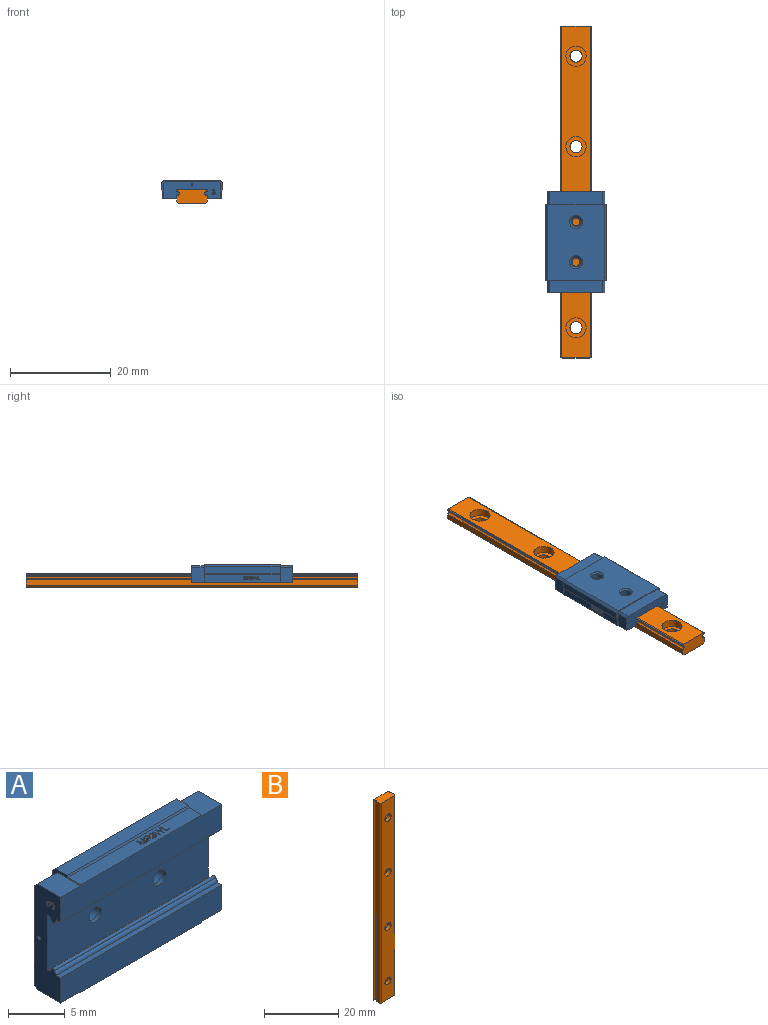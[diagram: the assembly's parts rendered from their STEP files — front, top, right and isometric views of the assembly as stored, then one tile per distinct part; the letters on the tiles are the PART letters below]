
ASSEMBLY  parts=2 mates=1
PART A: 248 faces, bbox 20.1x3.5x12 mm
  f0: cone r=1.3mm half-angle=45deg, axis (0,1,0), area 3.1mm2, adj f2,f9
  f1: cone r=1.3mm half-angle=45deg, axis (0,1,0), area 3.1mm2, adj f3,f9
  f2: cylinder r=1mm len=2mm, axis (0,1,0), area 6.9mm2, adj f0,f32
  f3: cylinder r=1mm len=2mm, axis (0,1,0), area 6.9mm2, adj f1,f33
  f4: cylinder r=0.15mm len=3mm, axis (-1,0,0), area 2.8mm2, adj f23,f76
  f5: cylinder r=0.15mm len=3mm, axis (1,0,0), area 2.8mm2, adj f28,f222
  f6: cylinder r=0.8mm len=1.6mm, axis (0,1,0), area 2mm2, adj f32,f51
  f7: cylinder r=0.8mm len=1.6mm, axis (0,1,0), area 2mm2, adj f33,f51
  f8: cylinder r=0.15mm len=20.1mm, axis (1,0,0), area 10.6mm2, adj f23,f28,f148,f223
  f9: plane 15.1x11.2mm, normal (0,1,0), area 158.5mm2, adj f0,f1,f10,f11,f12,f13
  f10: plane 12x3.5mm, normal (-1,0,0), area 3.7mm2, adj f9,f11,f13,f14,f15,f16,f17,f21
  f11: plane 15.1x0.4mm, normal (0,0.71,-0.71), area 8.5mm2, adj f9,f10,f12,f17
  f12: plane 12x3.5mm, normal (1,0,0), area 3.7mm2, adj f9,f11,f13,f17,f18,f19,f20,f21
  f13: plane 15.1x0.4mm, normal (0,0.71,0.71), area 8.5mm2, adj f9,f10,f12,f21
  f14: plane 2.9x2.5mm, normal (0,0,1), area 7.3mm2, adj f10,f22,f23,f24
  f15: plane 10.6x2.5mm, normal (0,1,0), area 26.5mm2, adj f10,f22,f23,f25
  f16: plane 2.9x2.5mm, normal (0,0,-1), area 7.3mm2, adj f10,f23,f25,f26
  f17: plane 15.1x1.4mm, normal (0,0,-1), area 21.1mm2, adj f10,f11,f12,f27
  f18: plane 2.9x2.5mm, normal (0,0,-1), area 7.3mm2, adj f12,f26,f28,f29
  f19: plane 2.9x2.5mm, normal (0,0,1), area 7.3mm2, adj f12,f24,f28,f30
  f20: plane 10.6x2.5mm, normal (0,1,0), area 26.5mm2, adj f12,f28,f29,f30
  f21: plane 15.1x1.4mm, normal (0,0,1), area 21.1mm2, adj f10,f12,f13,f31
  f22: plane 2.5x0.4mm, normal (0,0.71,0.71), area 1.4mm2, adj f10,f14,f15,f23
  f23: plane 11.4x3.3mm, normal (-1,0,0), area 27.5mm2, adj f4,f8,f14,f15,f16,f22,f24,f25
  f24: plane 20.1x2.8mm, normal (0,-1,0), area 55.8mm2, adj f10,f12,f14,f19,f23,f28,f52,f53
  f25: plane 2.5x0.4mm, normal (0,0.71,-0.71), area 1.4mm2, adj f10,f15,f16,f23
  f26: plane 20.1x2.8mm, normal (0,-1,0), area 55.8mm2, adj f10,f12,f16,f18,f23,f28,f54,f55
  f27: plane 15.1x0.2mm, normal (0,-0.87,-0.5), area 3.5mm2, adj f10,f12,f17,f54
  f28: plane 11.4x3.3mm, normal (1,0,0), area 27.5mm2, adj f5,f8,f18,f19,f20,f24,f26,f29
  f29: plane 2.5x0.4mm, normal (0,0.71,-0.71), area 1.4mm2, adj f12,f18,f20,f28
  f30: plane 2.5x0.4mm, normal (0,0.71,0.71), area 1.4mm2, adj f12,f19,f20,f28
  f31: plane 15.1x0.2mm, normal (0,-0.87,0.5), area 3.5mm2, adj f10,f12,f21,f52
  f32: plane 2x2mm, normal (0,1,0), area 1.1mm2, adj f2,f6
  f33: plane 2x2mm, normal (0,1,0), area 1.1mm2, adj f3,f7
  f34: bspline ~0.32x0.29mm, area 0.1mm2, adj f23,f35,f50,f73
  f35: plane 0.2x0.13mm, normal (0,-1,0.1), area 0mm2, adj f23,f34,f36,f73
  f36: bspline ~0.2x0.19mm, area 0.1mm2, adj f23,f35,f37,f73
  f37: bspline ~0.2x0.2mm, area 0.1mm2, adj f23,f36,f38,f73
  f38: bspline ~0.2x0.19mm, area 0.1mm2, adj f23,f37,f39,f73
  f39: bspline ~0.2x0.09mm, area 0mm2, adj f23,f38,f40,f73
  f40: plane 0.2x0.12mm, normal (0,-0.11,0.99), area 0mm2, adj f23,f39,f41,f73
  f41: bspline ~0.2x0.02mm, area 0mm2, adj f23,f40,f42,f73
  f42: bspline ~0.2x0.19mm, area 0.1mm2, adj f23,f41,f43,f73
  f43: bspline ~0.2x0.16mm, area 0mm2, adj f23,f42,f44,f73
  f44: bspline ~0.2x0.17mm, area 0.1mm2, adj f23,f43,f45,f73
  f45: plane 0.2x0.13mm, normal (0,1,0.1), area 0mm2, adj f23,f44,f46,f73
  f46: bspline ~0.3x0.26mm, area 0.1mm2, adj f23,f45,f47,f73
  f47: bspline ~0.29x0.26mm, area 0.1mm2, adj f23,f46,f48,f73
  f48: bspline ~0.2x0.2mm, area 0.1mm2, adj f23,f47,f49,f73
  f49: bspline ~0.25x0.2mm, area 0.1mm2, adj f23,f48,f50,f73
  f50: bspline ~0.34x0.32mm, area 0.1mm2, adj f23,f34,f49,f73
  f51: plane 20.1x6mm, normal (0,-1,0), area 116.6mm2, adj f6,f7,f23,f28,f74,f75
  f52: plane 15.1x1.58mm, normal (0,0,1), area 23mm2, adj f10,f12,f24,f31,f77,f78,f79,f80
  f53: plane 20.1x0.55mm, normal (0,0,-1), area 11.1mm2, adj f23,f24,f28,f148
  f54: plane 15.1x1.58mm, normal (0,0,-1), area 23mm2, adj f10,f12,f26,f27,f149,f150,f151,f152
  f55: plane 20.1x0.55mm, normal (0,0,1), area 11.1mm2, adj f23,f26,f28,f220
  f56: bspline ~0.32x0.29mm, area 0.1mm2, adj f28,f57,f72,f221
  f57: plane 0.2x0.13mm, normal (0,-1,-0.1), area 0mm2, adj f28,f56,f58,f221
  f58: bspline ~0.2x0.19mm, area 0.1mm2, adj f28,f57,f59,f221
  f59: bspline ~0.2x0.2mm, area 0.1mm2, adj f28,f58,f60,f221
  f60: bspline ~0.2x0.19mm, area 0.1mm2, adj f28,f59,f61,f221
  f61: bspline ~0.2x0.09mm, area 0mm2, adj f28,f60,f62,f221
  f62: plane 0.2x0.12mm, normal (0,-0.11,-0.99), area 0mm2, adj f28,f61,f63,f221
  f63: bspline ~0.2x0.02mm, area 0mm2, adj f28,f62,f64,f221
  f64: bspline ~0.2x0.19mm, area 0.1mm2, adj f28,f63,f65,f221
  f65: bspline ~0.2x0.16mm, area 0mm2, adj f28,f64,f66,f221
  f66: bspline ~0.2x0.17mm, area 0.1mm2, adj f28,f65,f67,f221
  f67: plane 0.2x0.13mm, normal (0,1,-0.1), area 0mm2, adj f28,f66,f68,f221
  f68: bspline ~0.3x0.26mm, area 0.1mm2, adj f28,f67,f69,f221
  f69: bspline ~0.29x0.26mm, area 0.1mm2, adj f28,f68,f70,f221
  f70: bspline ~0.2x0.2mm, area 0.1mm2, adj f28,f69,f71,f221
  f71: bspline ~0.25x0.2mm, area 0.1mm2, adj f28,f70,f72,f221
  f72: bspline ~0.34x0.32mm, area 0.1mm2, adj f28,f56,f71,f221
  f73: plane 1.04x0.66mm, normal (-1,0,0), area 0.3mm2, adj f34,f35,f36,f37,f38,f39,f40,f41
  f74: plane 20.1x0.35mm, normal (0,0,-1), area 7mm2, adj f23,f28,f51,f223
  f75: plane 20.1x0.35mm, normal (0,0,1), area 7mm2, adj f23,f28,f51,f224
  f76: plane 0.3x0.3mm, normal (-1,0,0), area 0.1mm2, adj f4
  f77: plane 0.33x0.15mm, normal (0,-1,0), area 0mm2, adj f52,f78,f82,f225
  f78: plane 0.62x0.15mm, normal (-1,0,0), area 0.1mm2, adj f52,f77,f79,f225
  f79: plane 0.15x0.1mm, normal (0,-1,0), area 0mm2, adj f52,f78,f80,f225
  f80: plane 0.7x0.15mm, normal (1,0,0), area 0.1mm2, adj f52,f79,f81,f225
  f81: plane 0.43x0.15mm, normal (0,1,0), area 0.1mm2, adj f52,f80,f82,f225
  f82: plane 0.15x0.08mm, normal (-1,0,0), area 0mm2, adj f52,f77,f81,f225
  f83: bspline ~0.17x0.15mm, area 0mm2, adj f52,f84,f99,f226
  f84: bspline ~0.15x0.14mm, area 0mm2, adj f52,f83,f85,f226
  f85: bspline ~0.2x0.18mm, area 0mm2, adj f52,f84,f86,f226
  f86: bspline ~0.2x0.18mm, area 0mm2, adj f52,f85,f87,f226
  f87: plane 0.15x0.09mm, normal (0.1,1,0), area 0mm2, adj f52,f86,f88,f226
  f88: bspline ~0.15x0.12mm, area 0mm2, adj f52,f87,f89,f226
  f89: bspline ~0.15x0.11mm, area 0mm2, adj f52,f88,f90,f226
  f90: bspline ~0.15x0.13mm, area 0mm2, adj f52,f89,f91,f226
  f91: bspline ~0.15x0.01mm, area 0mm2, adj f52,f90,f92,f226
  f92: plane 0.15x0.08mm, normal (0.99,-0.11,0), area 0mm2, adj f52,f91,f93,f226
  f93: bspline ~0.15x0.06mm, area 0mm2, adj f52,f92,f94,f226
  f94: bspline ~0.15x0.13mm, area 0mm2, adj f52,f93,f95,f226
  f95: bspline ~0.15x0.14mm, area 0mm2, adj f52,f94,f96,f226
  f96: bspline ~0.15x0.13mm, area 0mm2, adj f52,f95,f97,f226
  f97: plane 0.15x0.09mm, normal (0.1,-1,0), area 0mm2, adj f52,f96,f98,f226
  f98: bspline ~0.22x0.2mm, area 0mm2, adj f52,f97,f99,f226
  f99: bspline ~0.23x0.22mm, area 0.1mm2, adj f52,f83,f98,f226
  f100: plane 0.59x0.19mm, normal (0.95,0.3,0), area 0.1mm2, adj f52,f101,f114,f227
  f101: plane 0.15x0.1mm, normal (0,1,0), area 0mm2, adj f52,f100,f102,f227
  f102: plane 0.59x0.19mm, normal (-0.95,0.3,0), area 0.1mm2, adj f52,f101,f103,f227
  f103: plane 0.59x0.15mm, normal (1,0,0), area 0.1mm2, adj f52,f102,f104,f227
  f104: plane 0.15x0.1mm, normal (0,1,0), area 0mm2, adj f52,f103,f105,f227
  f105: plane 0.7x0.15mm, normal (-1,0,0), area 0.1mm2, adj f52,f104,f106,f227
  f106: plane 0.15x0.15mm, normal (0,-1,0), area 0mm2, adj f52,f105,f107,f227
  f107: plane 0.48x0.16mm, normal (0.95,-0.31,0), area 0.1mm2, adj f52,f106,f108,f227
  f108: bspline ~0.15x0.11mm, area 0mm2, adj f52,f107,f109,f227
  f109: bspline ~0.15x0.1mm, area 0mm2, adj f52,f108,f110,f227
  f110: plane 0.49x0.16mm, normal (-0.95,-0.3,0), area 0.1mm2, adj f52,f109,f111,f227
  f111: plane 0.15x0.15mm, normal (0,-1,0), area 0mm2, adj f52,f110,f112,f227
  f112: plane 0.7x0.15mm, normal (1,0,0), area 0.1mm2, adj f52,f111,f113,f227
  f113: plane 0.15x0.1mm, normal (0,1,0), area 0mm2, adj f52,f112,f114,f227
  f114: plane 0.59x0.15mm, normal (-1,0,0), area 0.1mm2, adj f52,f100,f113,f227
  f115: plane 0.15x0.1mm, normal (0,1,0), area 0mm2, adj f52,f116,f128,f228
  f116: bspline ~0.15x0.05mm, area 0mm2, adj f52,f115,f117,f228
  f117: bspline ~0.16x0.15mm, area 0mm2, adj f52,f116,f118,f228
  f118: plane 0.15x0.15mm, normal (0.86,0.51,0), area 0mm2, adj f52,f117,f119,f228
  f119: plane 0.15x0.11mm, normal (0,1,0), area 0mm2, adj f52,f118,f120,f228
  f120: plane 0.19x0.15mm, normal (-0.86,-0.51,0), area 0mm2, adj f52,f119,f121,f228
  f121: bspline ~0.15x0.1mm, area 0mm2, adj f52,f120,f122,f228
  f122: bspline ~0.15x0.05mm, area 0mm2, adj f52,f121,f123,f228
  f123: bspline ~0.19x0.19mm, area 0mm2, adj f52,f122,f124,f228
  f124: bspline ~0.23x0.19mm, area 0.1mm2, adj f52,f123,f125,f228
  f125: plane 0.3x0.15mm, normal (0,-1,0), area 0mm2, adj f52,f124,f126,f228
  f126: plane 0.7x0.15mm, normal (1,0,0), area 0.1mm2, adj f52,f125,f127,f228
  f127: plane 0.15x0.1mm, normal (0,1,0), area 0mm2, adj f52,f126,f128,f228
  f128: plane 0.31x0.15mm, normal (-1,0,0), area 0mm2, adj f52,f115,f127,f228
  f129: bspline ~0.15x0.09mm, area 0mm2, adj f52,f130,f147,f229
  f130: bspline ~0.15x0.08mm, area 0mm2, adj f52,f129,f131,f229
  f131: plane 0.54x0.15mm, normal (0.96,0.26,0), area 0.1mm2, adj f52,f130,f132,f229
  f132: plane 0.15x0.11mm, normal (0,1,0), area 0mm2, adj f52,f131,f133,f229
  f133: plane 0.7x0.18mm, normal (-0.97,0.24,0), area 0.1mm2, adj f52,f132,f134,f229
  f134: plane 0.15x0.1mm, normal (0,-1,0), area 0mm2, adj f52,f133,f135,f229
  f135: plane 0.46x0.15mm, normal (0.98,-0.22,0), area 0.1mm2, adj f52,f134,f136,f229
  f136: bspline ~0.15x0.14mm, area 0mm2, adj f52,f135,f137,f229
  f137: bspline ~0.25x0.15mm, area 0mm2, adj f52,f136,f138,f229
  f138: plane 0.35x0.15mm, normal (-0.96,-0.27,0), area 0.1mm2, adj f52,f137,f139,f229
  f139: plane 0.15x0.12mm, normal (0,-1,0), area 0mm2, adj f52,f138,f140,f229
  f140: plane 0.48x0.15mm, normal (0.96,-0.28,0), area 0.1mm2, adj f52,f139,f141,f229
  f141: bspline ~0.15x0.12mm, area 0mm2, adj f52,f140,f142,f229
  f142: bspline ~0.15x0.14mm, area 0mm2, adj f52,f141,f143,f229
  f143: plane 0.46x0.15mm, normal (-0.98,-0.22,0), area 0.1mm2, adj f52,f142,f144,f229
  f144: plane 0.15x0.1mm, normal (0,-1,0), area 0mm2, adj f52,f143,f145,f229
  f145: plane 0.7x0.18mm, normal (0.97,0.24,0), area 0.1mm2, adj f52,f144,f146,f229
  f146: plane 0.15x0.12mm, normal (0,1,0), area 0mm2, adj f52,f145,f147,f229
  f147: plane 0.52x0.15mm, normal (-0.96,0.28,0), area 0.1mm2, adj f52,f129,f146,f229
  f148: cylinder r=0.4mm len=20.1mm, axis (1,0,0), area 9.6mm2, adj f8,f23,f28,f53
  f149: plane 0.33x0.15mm, normal (0,-1,0), area 0mm2, adj f54,f150,f154,f230
  f150: plane 0.62x0.15mm, normal (1,0,0), area 0.1mm2, adj f54,f149,f151,f230
  f151: plane 0.15x0.1mm, normal (0,-1,0), area 0mm2, adj f54,f150,f152,f230
  f152: plane 0.7x0.15mm, normal (-1,0,0), area 0.1mm2, adj f54,f151,f153,f230
  f153: plane 0.43x0.15mm, normal (0,1,0), area 0.1mm2, adj f54,f152,f154,f230
  f154: plane 0.15x0.08mm, normal (1,0,0), area 0mm2, adj f54,f149,f153,f230
  f155: bspline ~0.17x0.15mm, area 0mm2, adj f54,f156,f171,f231
  f156: bspline ~0.15x0.14mm, area 0mm2, adj f54,f155,f157,f231
  f157: bspline ~0.2x0.18mm, area 0mm2, adj f54,f156,f158,f231
  f158: bspline ~0.2x0.18mm, area 0mm2, adj f54,f157,f159,f231
  f159: plane 0.15x0.09mm, normal (-0.1,1,0), area 0mm2, adj f54,f158,f160,f231
  f160: bspline ~0.15x0.12mm, area 0mm2, adj f54,f159,f161,f231
  f161: bspline ~0.15x0.11mm, area 0mm2, adj f54,f160,f162,f231
  f162: bspline ~0.15x0.13mm, area 0mm2, adj f54,f161,f163,f231
  f163: bspline ~0.15x0.01mm, area 0mm2, adj f54,f162,f164,f231
  f164: plane 0.15x0.08mm, normal (-0.99,-0.11,0), area 0mm2, adj f54,f163,f165,f231
  f165: bspline ~0.15x0.06mm, area 0mm2, adj f54,f164,f166,f231
  f166: bspline ~0.15x0.13mm, area 0mm2, adj f54,f165,f167,f231
  f167: bspline ~0.15x0.14mm, area 0mm2, adj f54,f166,f168,f231
  f168: bspline ~0.15x0.13mm, area 0mm2, adj f54,f167,f169,f231
  f169: plane 0.15x0.09mm, normal (-0.1,-1,0), area 0mm2, adj f54,f168,f170,f231
  f170: bspline ~0.22x0.2mm, area 0mm2, adj f54,f169,f171,f231
  f171: bspline ~0.23x0.22mm, area 0.1mm2, adj f54,f155,f170,f231
  f172: plane 0.59x0.19mm, normal (-0.95,0.3,0), area 0.1mm2, adj f54,f173,f186,f232
  f173: plane 0.15x0.1mm, normal (0,1,0), area 0mm2, adj f54,f172,f174,f232
  f174: plane 0.59x0.19mm, normal (0.95,0.3,0), area 0.1mm2, adj f54,f173,f175,f232
  f175: plane 0.59x0.15mm, normal (-1,0,0), area 0.1mm2, adj f54,f174,f176,f232
  f176: plane 0.15x0.1mm, normal (0,1,0), area 0mm2, adj f54,f175,f177,f232
  f177: plane 0.7x0.15mm, normal (1,0,0), area 0.1mm2, adj f54,f176,f178,f232
  f178: plane 0.15x0.15mm, normal (0,-1,0), area 0mm2, adj f54,f177,f179,f232
  f179: plane 0.48x0.16mm, normal (-0.95,-0.31,0), area 0.1mm2, adj f54,f178,f180,f232
  f180: bspline ~0.15x0.11mm, area 0mm2, adj f54,f179,f181,f232
  f181: bspline ~0.15x0.1mm, area 0mm2, adj f54,f180,f182,f232
  f182: plane 0.49x0.16mm, normal (0.95,-0.3,0), area 0.1mm2, adj f54,f181,f183,f232
  f183: plane 0.15x0.15mm, normal (0,-1,0), area 0mm2, adj f54,f182,f184,f232
  f184: plane 0.7x0.15mm, normal (-1,0,0), area 0.1mm2, adj f54,f183,f185,f232
  f185: plane 0.15x0.1mm, normal (0,1,0), area 0mm2, adj f54,f184,f186,f232
  f186: plane 0.59x0.15mm, normal (1,0,0), area 0.1mm2, adj f54,f172,f185,f232
  f187: plane 0.15x0.1mm, normal (0,1,0), area 0mm2, adj f54,f188,f200,f233
  f188: bspline ~0.15x0.05mm, area 0mm2, adj f54,f187,f189,f233
  f189: bspline ~0.16x0.15mm, area 0mm2, adj f54,f188,f190,f233
  f190: plane 0.15x0.15mm, normal (-0.86,0.51,0), area 0mm2, adj f54,f189,f191,f233
  f191: plane 0.15x0.11mm, normal (0,1,0), area 0mm2, adj f54,f190,f192,f233
  f192: plane 0.19x0.15mm, normal (0.86,-0.51,0), area 0mm2, adj f54,f191,f193,f233
  f193: bspline ~0.15x0.1mm, area 0mm2, adj f54,f192,f194,f233
  f194: bspline ~0.15x0.05mm, area 0mm2, adj f54,f193,f195,f233
  f195: bspline ~0.19x0.19mm, area 0mm2, adj f54,f194,f196,f233
  f196: bspline ~0.23x0.19mm, area 0.1mm2, adj f54,f195,f197,f233
  f197: plane 0.3x0.15mm, normal (0,-1,0), area 0mm2, adj f54,f196,f198,f233
  f198: plane 0.7x0.15mm, normal (-1,0,0), area 0.1mm2, adj f54,f197,f199,f233
  f199: plane 0.15x0.1mm, normal (0,1,0), area 0mm2, adj f54,f198,f200,f233
  f200: plane 0.31x0.15mm, normal (1,0,0), area 0mm2, adj f54,f187,f199,f233
  f201: bspline ~0.15x0.09mm, area 0mm2, adj f54,f202,f219,f234
  f202: bspline ~0.15x0.08mm, area 0mm2, adj f54,f201,f203,f234
  f203: plane 0.54x0.15mm, normal (-0.96,0.26,0), area 0.1mm2, adj f54,f202,f204,f234
  f204: plane 0.15x0.11mm, normal (0,1,0), area 0mm2, adj f54,f203,f205,f234
  f205: plane 0.7x0.18mm, normal (0.97,0.24,0), area 0.1mm2, adj f54,f204,f206,f234
  f206: plane 0.15x0.1mm, normal (0,-1,0), area 0mm2, adj f54,f205,f207,f234
  f207: plane 0.46x0.15mm, normal (-0.98,-0.22,0), area 0.1mm2, adj f54,f206,f208,f234
  f208: bspline ~0.15x0.14mm, area 0mm2, adj f54,f207,f209,f234
  f209: bspline ~0.25x0.15mm, area 0mm2, adj f54,f208,f210,f234
  f210: plane 0.35x0.15mm, normal (0.96,-0.27,0), area 0.1mm2, adj f54,f209,f211,f234
  f211: plane 0.15x0.12mm, normal (0,-1,0), area 0mm2, adj f54,f210,f212,f234
  f212: plane 0.48x0.15mm, normal (-0.96,-0.28,0), area 0.1mm2, adj f54,f211,f213,f234
  f213: bspline ~0.15x0.12mm, area 0mm2, adj f54,f212,f214,f234
  f214: bspline ~0.15x0.14mm, area 0mm2, adj f54,f213,f215,f234
  f215: plane 0.46x0.15mm, normal (0.98,-0.22,0), area 0.1mm2, adj f54,f214,f216,f234
  f216: plane 0.15x0.1mm, normal (0,-1,0), area 0mm2, adj f54,f215,f217,f234
  f217: plane 0.7x0.18mm, normal (-0.97,0.24,0), area 0.1mm2, adj f54,f216,f218,f234
  f218: plane 0.15x0.12mm, normal (0,1,0), area 0mm2, adj f54,f217,f219,f234
  f219: plane 0.52x0.15mm, normal (0.96,0.28,0), area 0.1mm2, adj f54,f201,f218,f234
  f220: cylinder r=0.4mm len=20.1mm, axis (1,0,0), area 9.6mm2, adj f23,f28,f55,f235
  f221: plane 1.04x0.66mm, normal (1,0,0), area 0.3mm2, adj f56,f57,f58,f59,f60,f61,f62,f63
  f222: plane 0.3x0.3mm, normal (1,0,0), area 0.1mm2, adj f5
  f223: cylinder r=0.4mm len=20.1mm, axis (1,0,0), area 9.6mm2, adj f8,f23,f28,f74
  f224: cylinder r=0.4mm len=20.1mm, axis (1,0,0), area 9.6mm2, adj f23,f28,f75,f235
  f225: plane 0.7x0.43mm, normal (0,0,1), area 0.1mm2, adj f77,f78,f79,f80,f81,f82
  f226: plane 0.71x0.45mm, normal (0,0,1), area 0.1mm2, adj f83,f84,f85,f86,f87,f88,f89,f90
  f227: plane 0.7x0.67mm, normal (0,0,1), area 0.2mm2, adj f100,f101,f102,f103,f104,f105,f106,f107
  f228: plane 0.7x0.6mm, normal (0,0,1), area 0.2mm2, adj f115,f116,f117,f118,f119,f120,f121,f122
  f229: plane 0.92x0.7mm, normal (0,0,1), area 0.2mm2, adj f129,f130,f131,f132,f133,f134,f135,f136
  f230: plane 0.7x0.43mm, normal (0,0,-1), area 0.1mm2, adj f149,f150,f151,f152,f153,f154
  f231: plane 0.71x0.45mm, normal (0,0,-1), area 0.1mm2, adj f155,f156,f157,f158,f159,f160,f161,f162
  f232: plane 0.7x0.67mm, normal (0,0,-1), area 0.2mm2, adj f172,f173,f174,f175,f176,f177,f178,f179
  f233: plane 0.7x0.6mm, normal (0,0,-1), area 0.2mm2, adj f187,f188,f189,f190,f191,f192,f193,f194
  f234: plane 0.92x0.7mm, normal (0,0,-1), area 0.2mm2, adj f201,f202,f203,f204,f205,f206,f207,f208
  f235: cylinder r=0.15mm len=20.1mm, axis (1,0,0), area 10.6mm2, adj f23,f28,f220,f224
  f236: plane 0.22x0.15mm, normal (-1,0,0), area 0mm2, adj f228,f237,f240,f246
  f237: plane 0.19x0.15mm, normal (0,-1,0), area 0mm2, adj f228,f236,f238,f246
  f238: bspline ~0.15x0.15mm, area 0mm2, adj f228,f237,f239,f246
  f239: bspline ~0.15x0.13mm, area 0mm2, adj f228,f238,f240,f246
  f240: plane 0.21x0.15mm, normal (0,1,0), area 0mm2, adj f228,f236,f239,f246
  f241: plane 0.22x0.15mm, normal (1,0,0), area 0mm2, adj f233,f242,f245,f247
  f242: plane 0.19x0.15mm, normal (0,-1,0), area 0mm2, adj f233,f241,f243,f247
  f243: bspline ~0.15x0.15mm, area 0mm2, adj f233,f242,f244,f247
  f244: bspline ~0.15x0.13mm, area 0mm2, adj f233,f243,f245,f247
  f245: plane 0.21x0.15mm, normal (0,1,0), area 0mm2, adj f233,f241,f244,f247
  f246: plane 0.34x0.22mm, normal (0,0,1), area 0.1mm2, adj f236,f237,f238,f239,f240
  f247: plane 0.34x0.22mm, normal (0,0,-1), area 0.1mm2, adj f241,f242,f243,f244,f245
PART B: 30 faces, bbox 6x2.7x66 mm
  f0: cylinder r=2mm len=4mm, axis (0,-1,0), area 18.8mm2, adj f12,f29
  f1: cylinder r=1.2mm len=2.4mm, axis (0,-1,0), area 9mm2, adj f20,f29
  f2: cylinder r=2mm len=4mm, axis (0,-1,0), area 18.8mm2, adj f12,f28
  f3: cylinder r=1.2mm len=2.4mm, axis (0,-1,0), area 9mm2, adj f20,f28
  f4: cylinder r=2mm len=4mm, axis (0,-1,0), area 18.8mm2, adj f12,f27
  f5: cylinder r=1.2mm len=2.4mm, axis (0,-1,0), area 9mm2, adj f20,f27
  f6: cylinder r=2mm len=4mm, axis (0,-1,0), area 18.8mm2, adj f12,f26
  f7: cylinder r=1.2mm len=2.4mm, axis (0,-1,0), area 9mm2, adj f20,f26
  f8: cylinder r=0.15mm len=66mm, axis (0,0,-1), area 34.8mm2, adj f9,f23,f24,f25
  f9: cylinder r=0.4mm len=66mm, axis (0,0,-1), area 31.5mm2, adj f8,f10,f24,f25
  f10: plane 66x0.2mm, normal (1,0,0), area 13.2mm2, adj f9,f11,f24,f25
  f11: cylinder r=0.15mm len=66mm, axis (0,0,-1), area 15.6mm2, adj f10,f12,f24,f25
  f12: plane 66x5.7mm, normal (0,1,0), area 325.9mm2, adj f0,f2,f4,f6,f11,f13,f24,f25
  f13: cylinder r=0.15mm len=66mm, axis (0,0,-1), area 15.6mm2, adj f12,f14,f24,f25
  f14: plane 66x0.2mm, normal (-1,0,0), area 13.2mm2, adj f13,f15,f24,f25
  f15: cylinder r=0.4mm len=66mm, axis (0,0,-1), area 31.5mm2, adj f14,f16,f24,f25
  f16: cylinder r=0.15mm len=66mm, axis (0,0,-1), area 34.8mm2, adj f15,f17,f24,f25
  f17: cylinder r=0.4mm len=66mm, axis (0,0,-1), area 31.5mm2, adj f16,f18,f24,f25
  f18: plane 66x1.15mm, normal (-1,0,0), area 75.9mm2, adj f17,f19,f24,f25
  f19: plane 66x0.4mm, normal (-0.71,-0.71,0), area 37.3mm2, adj f18,f20,f24,f25
  f20: plane 66x5.2mm, normal (0,-1,0), area 325.1mm2, adj f1,f3,f5,f7,f19,f21,f24,f25
  f21: plane 66x0.4mm, normal (0.71,-0.71,0), area 37.3mm2, adj f20,f22,f24,f25
  f22: plane 66x1.15mm, normal (1,0,0), area 75.9mm2, adj f21,f23,f24,f25
  f23: cylinder r=0.4mm len=66mm, axis (0,0,-1), area 31.5mm2, adj f8,f22,f24,f25
  f24: plane 6x2.7mm, normal (0,0,1), area 15.5mm2, adj f8,f9,f10,f11,f12,f13,f14,f15
  f25: plane 6x2.7mm, normal (0,0,-1), area 15.5mm2, adj f8,f9,f10,f11,f12,f13,f14,f15
  f26: plane 4x4mm, normal (0,1,0), area 8mm2, adj f6,f7
  f27: plane 4x4mm, normal (0,1,0), area 8mm2, adj f4,f5
  f28: plane 4x4mm, normal (0,1,0), area 8mm2, adj f2,f3
  f29: plane 4x4mm, normal (0,1,0), area 8mm2, adj f0,f1
PLACE A rot(axis=(0.58,0.58,0.58),120deg) t=(0,17.08,0.05)mm
PLACE B rot(axis=(1,0,0),90deg) t=(0,10.05,2.75)mm fixed
MATE slider A.f235 <-> B.f16  axis (0,1,0) through (-2.6,-32.92,2)mm
